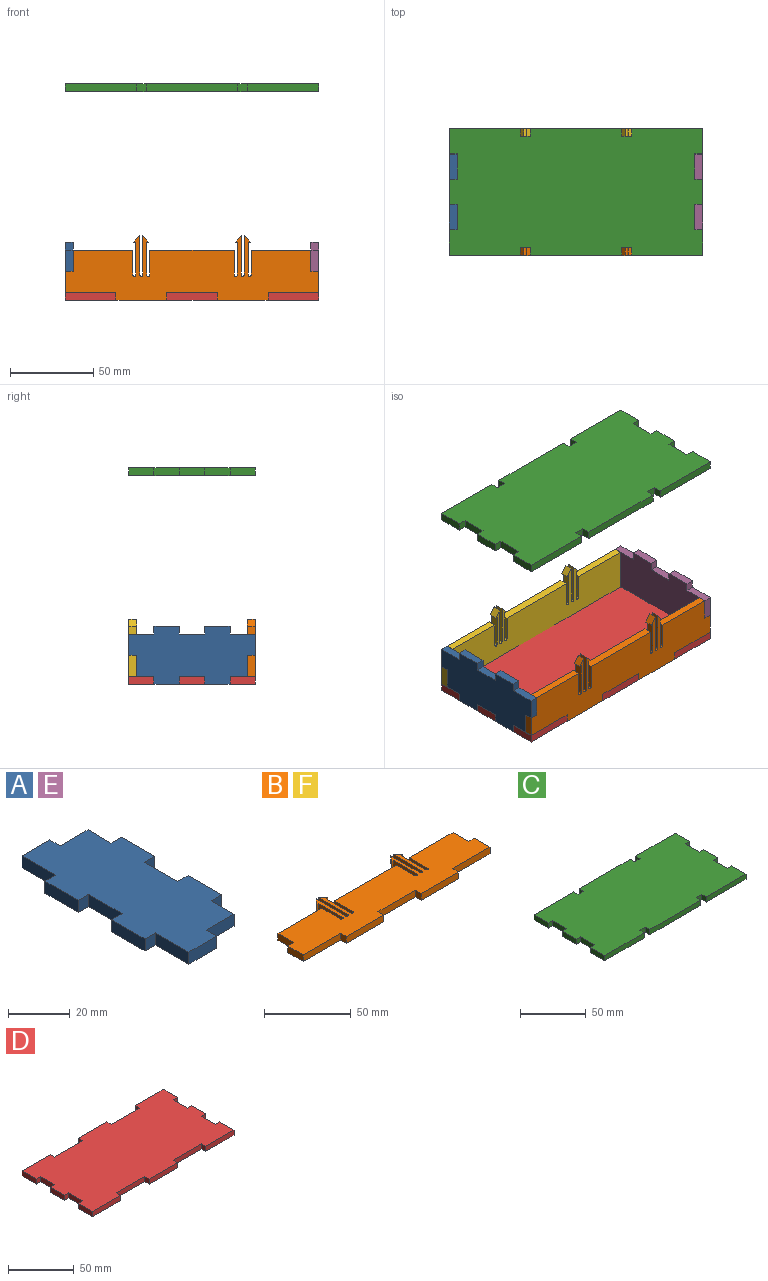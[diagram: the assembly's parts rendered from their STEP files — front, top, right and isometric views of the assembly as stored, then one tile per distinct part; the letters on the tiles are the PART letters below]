
ASSEMBLY  parts=6 mates=5
PART A: 26 faces, bbox 34.9x76.2x4.8 mm
  f0: plane 12.7x4.76mm, normal (0,1,0), area 60.5mm2, adj f1,f23,f24,f25
  f1: plane 4.76x4.76mm, normal (1,0,0), area 22.7mm2, adj f0,f2,f24,f25
  f2: plane 12.7x4.76mm, normal (0,1,0), area 60.5mm2, adj f1,f3,f24,f25
  f3: plane 15.24x4.76mm, normal (-1,0,0), area 72.6mm2, adj f2,f4,f24,f25
  f4: plane 4.76x4.76mm, normal (0,1,0), area 22.7mm2, adj f3,f5,f24,f25
  f5: plane 15.24x4.76mm, normal (-1,0,0), area 72.6mm2, adj f4,f6,f24,f25
  f6: plane 4.76x4.76mm, normal (0,-1,0), area 22.7mm2, adj f5,f7,f24,f25
  f7: plane 15.24x4.76mm, normal (-1,0,0), area 72.6mm2, adj f6,f8,f24,f25
  f8: plane 4.76x4.76mm, normal (0,1,0), area 22.7mm2, adj f7,f9,f24,f25
  f9: plane 15.24x4.76mm, normal (-1,0,0), area 72.6mm2, adj f8,f10,f24,f25
  f10: plane 4.76x4.76mm, normal (0,-1,0), area 22.7mm2, adj f9,f11,f24,f25
  f11: plane 15.24x4.76mm, normal (-1,0,0), area 72.6mm2, adj f10,f12,f24,f25
  f12: plane 12.7x4.76mm, normal (0,-1,0), area 60.5mm2, adj f11,f13,f24,f25
  f13: plane 4.76x4.76mm, normal (1,0,0), area 22.7mm2, adj f12,f14,f24,f25
  f14: plane 12.7x4.76mm, normal (0,-1,0), area 60.5mm2, adj f13,f15,f24,f25
  f15: plane 10.48x4.76mm, normal (1,0,0), area 49.9mm2, adj f14,f16,f24,f25
  f16: plane 4.76x4.76mm, normal (0,-1,0), area 22.7mm2, adj f15,f17,f24,f25
  f17: plane 15.24x4.76mm, normal (1,0,0), area 72.6mm2, adj f16,f18,f24,f25
  f18: plane 4.76x4.76mm, normal (0,1,0), area 22.7mm2, adj f17,f19,f24,f25
  f19: plane 15.24x4.76mm, normal (1,0,0), area 72.6mm2, adj f18,f20,f24,f25
  f20: plane 4.76x4.76mm, normal (0,-1,0), area 22.7mm2, adj f19,f21,f24,f25
  f21: plane 15.24x4.76mm, normal (1,0,0), area 72.6mm2, adj f20,f22,f24,f25
  f22: plane 4.76x4.76mm, normal (0,1,0), area 22.7mm2, adj f21,f23,f24,f25
  f23: plane 10.48x4.76mm, normal (1,0,0), area 49.9mm2, adj f0,f22,f24,f25
  f24: plane 76.2x34.93mm, normal (0,0,1), area 2104.8mm2, adj f0,f1,f2,f3,f4,f5,f6,f7
  f25: plane 76.2x34.93mm, normal (0,0,-1), area 2104.8mm2, adj f0,f1,f2,f3,f4,f5,f6,f7
PART B: 46 faces, bbox 152.4x39.1x4.8 mm
  f0: cylinder r=0.95mm len=4.76mm, axis (0,0,-1), area 14.2mm2, adj f1,f43,f44,f45
  f1: plane 23.96x4.76mm, normal (1,0,0), area 114.1mm2, adj f0,f2,f44,f45
  f2: plane 4.76x4.2mm, normal (-0.76,0.65,0), area 26.3mm2, adj f1,f3,f44,f45
  f3: plane 4.76x1.3mm, normal (0,-1,0), area 6.2mm2, adj f2,f4,f44,f45
  f4: plane 19.76x4.76mm, normal (-1,0,0), area 94.1mm2, adj f3,f5,f44,f45
  f5: cylinder r=0.95mm len=4.76mm, axis (0,0,-1), area 14.2mm2, adj f4,f6,f44,f45
  f6: plane 15x4.76mm, normal (1,0,0), area 71.4mm2, adj f5,f7,f44,f45
  f7: plane 50.66x4.76mm, normal (0,1,0), area 241.3mm2, adj f6,f8,f44,f45
  f8: plane 15x4.76mm, normal (-1,0,0), area 71.4mm2, adj f7,f9,f44,f45
  f9: cylinder r=0.95mm len=4.76mm, axis (0,0,-1), area 14.2mm2, adj f8,f10,f44,f45
  f10: plane 19.76x4.76mm, normal (1,0,0), area 94.1mm2, adj f9,f11,f44,f45
  f11: plane 4.76x1.3mm, normal (0,-1,0), area 6.2mm2, adj f10,f12,f44,f45
  f12: plane 4.76x4.2mm, normal (0.76,0.65,0), area 26.3mm2, adj f11,f13,f44,f45
  f13: plane 23.96x4.76mm, normal (-1,0,0), area 114.1mm2, adj f12,f14,f44,f45
  f14: cylinder r=0.95mm len=4.76mm, axis (0,0,-1), area 14.2mm2, adj f13,f15,f44,f45
  f15: plane 23.96x4.76mm, normal (1,0,0), area 114.1mm2, adj f14,f16,f44,f45
  f16: plane 4.76x4.2mm, normal (-0.76,0.65,0), area 26.3mm2, adj f15,f17,f44,f45
  f17: plane 4.76x1.3mm, normal (0,-1,0), area 6.2mm2, adj f16,f18,f44,f45
  f18: plane 19.76x4.76mm, normal (-1,0,0), area 94.1mm2, adj f17,f19,f44,f45
  f19: cylinder r=0.95mm len=4.76mm, axis (0,0,-1), area 14.2mm2, adj f18,f20,f44,f45
  f20: plane 15x4.76mm, normal (1,0,0), area 71.4mm2, adj f19,f21,f44,f45
  f21: plane 35.81x4.76mm, normal (0,1,0), area 170.5mm2, adj f20,f22,f44,f45
  f22: plane 12.7x4.76mm, normal (-1,0,0), area 60.5mm2, adj f21,f23,f44,f45
  f23: plane 4.76x4.76mm, normal (0,1,0), area 22.7mm2, adj f22,f24,f44,f45
  f24: plane 12.7x4.76mm, normal (-1,0,0), area 60.5mm2, adj f23,f25,f44,f45
  f25: plane 30.48x4.76mm, normal (0,-1,0), area 145.2mm2, adj f24,f26,f44,f45
  f26: plane 4.76x4.76mm, normal (-1,0,0), area 22.7mm2, adj f25,f27,f44,f45
  f27: plane 30.48x4.76mm, normal (0,-1,0), area 145.2mm2, adj f26,f28,f44,f45
  f28: plane 4.76x4.76mm, normal (1,0,0), area 22.7mm2, adj f27,f29,f44,f45
  f29: plane 30.48x4.76mm, normal (0,-1,0), area 145.2mm2, adj f28,f30,f44,f45
  f30: plane 4.76x4.76mm, normal (-1,0,0), area 22.7mm2, adj f29,f31,f44,f45
  f31: plane 30.48x4.76mm, normal (0,-1,0), area 145.2mm2, adj f30,f32,f44,f45
  f32: plane 4.76x4.76mm, normal (1,0,0), area 22.7mm2, adj f31,f33,f44,f45
  f33: plane 30.48x4.76mm, normal (0,-1,0), area 145.2mm2, adj f32,f34,f44,f45
  f34: plane 12.7x4.76mm, normal (1,0,0), area 60.5mm2, adj f33,f35,f44,f45
  f35: plane 4.76x4.76mm, normal (0,1,0), area 22.7mm2, adj f34,f36,f44,f45
  f36: plane 12.7x4.76mm, normal (1,0,0), area 60.5mm2, adj f35,f37,f44,f45
  f37: plane 35.81x4.76mm, normal (0,1,0), area 170.5mm2, adj f36,f38,f44,f45
  f38: plane 15x4.76mm, normal (-1,0,0), area 71.4mm2, adj f37,f39,f44,f45
  f39: cylinder r=0.95mm len=4.76mm, axis (0,0,-1), area 14.2mm2, adj f38,f40,f44,f45
  f40: plane 19.76x4.76mm, normal (1,0,0), area 94.1mm2, adj f39,f41,f44,f45
  f41: plane 4.76x1.3mm, normal (0,-1,0), area 6.2mm2, adj f40,f42,f44,f45
  f42: plane 4.76x4.2mm, normal (0.76,0.65,0), area 26.3mm2, adj f41,f43,f44,f45
  f43: plane 23.96x4.76mm, normal (-1,0,0), area 114.1mm2, adj f0,f42,f44,f45
  f44: plane 152.4x39.13mm, normal (0,0,1), area 3934.9mm2, adj f0,f1,f2,f3,f4,f5,f6,f7
  f45: plane 152.4x39.13mm, normal (0,0,-1), area 3934.9mm2, adj f0,f1,f2,f3,f4,f5,f6,f7
PART C: 38 faces, bbox 152.4x76.2x4.8 mm
  f0: plane 4.76x4.76mm, normal (0,1,0), area 22.7mm2, adj f1,f35,f36,f37
  f1: plane 15.24x4.76mm, normal (1,0,0), area 72.6mm2, adj f0,f2,f36,f37
  f2: plane 4.76x4.76mm, normal (0,-1,0), area 22.7mm2, adj f1,f3,f36,f37
  f3: plane 15.24x4.76mm, normal (1,0,0), area 72.6mm2, adj f2,f4,f36,f37
  f4: plane 4.76x4.76mm, normal (0,1,0), area 22.7mm2, adj f3,f5,f36,f37
  f5: plane 15.24x4.76mm, normal (1,0,0), area 72.6mm2, adj f4,f6,f36,f37
  f6: plane 4.76x4.76mm, normal (0,-1,0), area 22.7mm2, adj f5,f7,f36,f37
  f7: plane 15.24x4.76mm, normal (1,0,0), area 72.6mm2, adj f6,f8,f36,f37
  f8: plane 42.72x4.76mm, normal (0,1,0), area 203.5mm2, adj f7,f9,f36,f37
  f9: plane 4.76x4.76mm, normal (-1,0,0), area 22.7mm2, adj f8,f10,f36,f37
  f10: plane 6x4.76mm, normal (0,1,0), area 28.6mm2, adj f9,f11,f36,f37
  f11: plane 4.76x4.76mm, normal (1,0,0), area 22.7mm2, adj f10,f12,f36,f37
  f12: plane 54.96x4.76mm, normal (0,1,0), area 261.7mm2, adj f11,f13,f36,f37
  f13: plane 4.76x4.76mm, normal (-1,0,0), area 22.7mm2, adj f12,f14,f36,f37
  f14: plane 6x4.76mm, normal (0,1,0), area 28.6mm2, adj f13,f15,f36,f37
  f15: plane 4.76x4.76mm, normal (1,0,0), area 22.7mm2, adj f14,f16,f36,f37
  f16: plane 42.72x4.76mm, normal (0,1,0), area 203.5mm2, adj f15,f17,f36,f37
  f17: plane 15.24x4.76mm, normal (-1,0,0), area 72.6mm2, adj f16,f18,f36,f37
  f18: plane 4.76x4.76mm, normal (0,-1,0), area 22.7mm2, adj f17,f19,f36,f37
  f19: plane 15.24x4.76mm, normal (-1,0,0), area 72.6mm2, adj f18,f20,f36,f37
  f20: plane 4.76x4.76mm, normal (0,1,0), area 22.7mm2, adj f19,f21,f36,f37
  f21: plane 15.24x4.76mm, normal (-1,0,0), area 72.6mm2, adj f20,f22,f36,f37
  f22: plane 4.76x4.76mm, normal (0,-1,0), area 22.7mm2, adj f21,f23,f36,f37
  f23: plane 15.24x4.76mm, normal (-1,0,0), area 72.6mm2, adj f22,f24,f36,f37
  f24: plane 4.76x4.76mm, normal (0,1,0), area 22.7mm2, adj f23,f25,f36,f37
  f25: plane 15.24x4.76mm, normal (-1,0,0), area 72.6mm2, adj f24,f26,f36,f37
  f26: plane 42.72x4.76mm, normal (0,-1,0), area 203.5mm2, adj f25,f27,f36,f37
  f27: plane 4.76x4.76mm, normal (1,0,0), area 22.7mm2, adj f26,f28,f36,f37
  f28: plane 6x4.76mm, normal (0,-1,0), area 28.6mm2, adj f27,f29,f36,f37
  f29: plane 4.76x4.76mm, normal (-1,0,0), area 22.7mm2, adj f28,f30,f36,f37
  f30: plane 54.96x4.76mm, normal (0,-1,0), area 261.7mm2, adj f29,f31,f36,f37
  f31: plane 4.76x4.76mm, normal (1,0,0), area 22.7mm2, adj f30,f32,f36,f37
  f32: plane 6x4.76mm, normal (0,-1,0), area 28.6mm2, adj f31,f33,f36,f37
  f33: plane 4.76x4.76mm, normal (-1,0,0), area 22.7mm2, adj f32,f34,f36,f37
  f34: plane 42.72x4.76mm, normal (0,-1,0), area 203.5mm2, adj f33,f35,f36,f37
  f35: plane 15.24x4.76mm, normal (1,0,0), area 72.6mm2, adj f0,f34,f36,f37
  f36: plane 152.4x76.2mm, normal (0,0,1), area 11208.3mm2, adj f0,f1,f2,f3,f4,f5,f6,f7
  f37: plane 152.4x76.2mm, normal (0,0,-1), area 11208.3mm2, adj f0,f1,f2,f3,f4,f5,f6,f7
PART D: 38 faces, bbox 152.4x76.2x4.8 mm
  f0: plane 4.76x4.76mm, normal (0,1,0), area 22.7mm2, adj f1,f35,f36,f37
  f1: plane 15.24x4.76mm, normal (1,0,0), area 72.6mm2, adj f0,f2,f36,f37
  f2: plane 4.76x4.76mm, normal (0,-1,0), area 22.7mm2, adj f1,f3,f36,f37
  f3: plane 15.24x4.76mm, normal (1,0,0), area 72.6mm2, adj f2,f4,f36,f37
  f4: plane 30.48x4.76mm, normal (0,1,0), area 145.2mm2, adj f3,f5,f36,f37
  f5: plane 4.76x4.76mm, normal (-1,0,0), area 22.7mm2, adj f4,f6,f36,f37
  f6: plane 30.48x4.76mm, normal (0,1,0), area 145.2mm2, adj f5,f7,f36,f37
  f7: plane 4.76x4.76mm, normal (1,0,0), area 22.7mm2, adj f6,f8,f36,f37
  f8: plane 30.48x4.76mm, normal (0,1,0), area 145.2mm2, adj f7,f9,f36,f37
  f9: plane 4.76x4.76mm, normal (-1,0,0), area 22.7mm2, adj f8,f10,f36,f37
  f10: plane 30.48x4.76mm, normal (0,1,0), area 145.2mm2, adj f9,f11,f36,f37
  f11: plane 4.76x4.76mm, normal (1,0,0), area 22.7mm2, adj f10,f12,f36,f37
  f12: plane 30.48x4.76mm, normal (0,1,0), area 145.2mm2, adj f11,f13,f36,f37
  f13: plane 15.24x4.76mm, normal (-1,0,0), area 72.6mm2, adj f12,f14,f36,f37
  f14: plane 4.76x4.76mm, normal (0,-1,0), area 22.7mm2, adj f13,f15,f36,f37
  f15: plane 15.24x4.76mm, normal (-1,0,0), area 72.6mm2, adj f14,f16,f36,f37
  f16: plane 4.76x4.76mm, normal (0,1,0), area 22.7mm2, adj f15,f17,f36,f37
  f17: plane 15.24x4.76mm, normal (-1,0,0), area 72.6mm2, adj f16,f18,f36,f37
  f18: plane 4.76x4.76mm, normal (0,-1,0), area 22.7mm2, adj f17,f19,f36,f37
  f19: plane 15.24x4.76mm, normal (-1,0,0), area 72.6mm2, adj f18,f20,f36,f37
  f20: plane 4.76x4.76mm, normal (0,1,0), area 22.7mm2, adj f19,f21,f36,f37
  f21: plane 15.24x4.76mm, normal (-1,0,0), area 72.6mm2, adj f20,f22,f36,f37
  f22: plane 30.48x4.76mm, normal (0,-1,0), area 145.2mm2, adj f21,f23,f36,f37
  f23: plane 4.76x4.76mm, normal (1,0,0), area 22.7mm2, adj f22,f24,f36,f37
  f24: plane 30.48x4.76mm, normal (0,-1,0), area 145.2mm2, adj f23,f25,f36,f37
  f25: plane 4.76x4.76mm, normal (-1,0,0), area 22.7mm2, adj f24,f26,f36,f37
  f26: plane 30.48x4.76mm, normal (0,-1,0), area 145.2mm2, adj f25,f27,f36,f37
  f27: plane 4.76x4.76mm, normal (1,0,0), area 22.7mm2, adj f26,f28,f36,f37
  f28: plane 30.48x4.76mm, normal (0,-1,0), area 145.2mm2, adj f27,f29,f36,f37
  f29: plane 4.76x4.76mm, normal (-1,0,0), area 22.7mm2, adj f28,f30,f36,f37
  f30: plane 30.48x4.76mm, normal (0,-1,0), area 145.2mm2, adj f29,f31,f36,f37
  f31: plane 15.24x4.76mm, normal (1,0,0), area 72.6mm2, adj f30,f32,f36,f37
  f32: plane 4.76x4.76mm, normal (0,1,0), area 22.7mm2, adj f31,f33,f36,f37
  f33: plane 15.24x4.76mm, normal (1,0,0), area 72.6mm2, adj f32,f34,f36,f37
  f34: plane 4.76x4.76mm, normal (0,-1,0), area 22.7mm2, adj f33,f35,f36,f37
  f35: plane 15.24x4.76mm, normal (1,0,0), area 72.6mm2, adj f0,f34,f36,f37
  f36: plane 152.4x76.2mm, normal (0,0,1), area 10741.9mm2, adj f0,f1,f2,f3,f4,f5,f6,f7
  f37: plane 152.4x76.2mm, normal (0,0,-1), area 10741.9mm2, adj f0,f1,f2,f3,f4,f5,f6,f7
PART E: same geometry as A
PART F: same geometry as B
PLACE A rot(axis=(0,1,0),90deg) t=(-35.95,-14.1,-13.94)mm
PLACE B rot(axis=(1,0,0),90deg) t=(-35.95,-9.34,-90.14)mm
PLACE C t=(-35.95,-158.57,124.2)mm
PLACE D t=(-35.95,-14.1,-1.24)mm fixed
PLACE E rot(axis=(0,1,0),90deg) t=(111.69,-14.1,-13.94)mm
PLACE F rot(axis=(1,0,0),90deg) t=(-35.95,62.1,-90.14)mm
MATE fastened A.f25 <-> D.f13  axis (-1,0,0) through (-35.95,46.86,3.52)mm
MATE fastened F.f45 <-> D.f12  axis (0,1,0) through (-35.95,62.1,3.52)mm
MATE slider C.f36 <-> A.f11  axis (0,0,1) through (-35.95,-14.1,128.96)mm
MATE fastened E.f24 <-> D.f31  axis (1,0,0) through (116.45,1.14,3.52)mm
MATE fastened B.f33 <-> D.f36  axis (0,0,1) through (116.45,-14.1,3.52)mm
